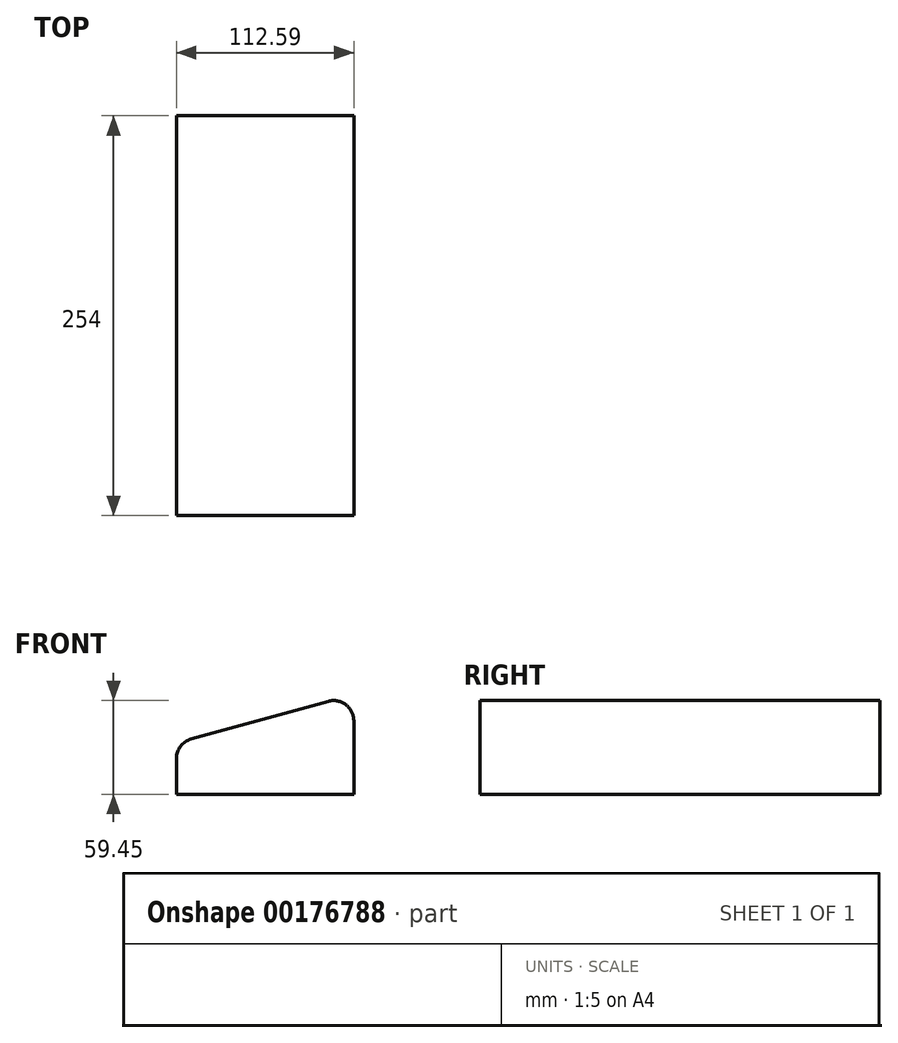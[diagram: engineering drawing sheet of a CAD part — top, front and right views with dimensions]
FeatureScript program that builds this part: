
annotation { "Feature Type Name" : "Feature", "Feature Type Description" : "" }
export const myFeature = defineFeature(function(context is Context, id is Id, definition is map)
    precondition{}
    {
        {
            var Q0;
            Q0=qCreatedBy(makeId("Front.planeOp"),FACE);
            var sketch = newSketch(context, id + "F0", { "sketchPlane" : qUnion([Q0])});
            skLineSegment(sketch, "E0", {"start": v(-38.25, 0) * mm, "end": v(-38.25, 22.78) * mm});
            skLineSegment(sketch, "E1", {"start": v(-28.92, 35.02) * mm, "end": v(58.28, 59) * mm});
            skLineSegment(sketch, "E2", {"start": v(74.34, 46.75) * mm, "end": v(74.34, 0) * mm});
            skLineSegment(sketch, "E3", {"start": v(74.34, 0) * mm, "end": v(-38.25, 0) * mm});
            skPoint(sketch, "E4.visualSharp", {"position": v(-38.25, 32.46) * mm});
            skArc(sketch, "E4.filletArc", {"start": v(-28.92, 35.02) * mm, "mid": v(-35.65, 30.48) * mm, "end": v(-38.25, 22.78) * mm});
            skPoint(sketch, "E5.visualSharp", {"position": v(74.34, 63.4) * mm});
            skArc(sketch, "E5.filletArc", {"start": v(74.34, 46.75) * mm, "mid": v(69.34, 56.85) * mm, "end": v(58.28, 59) * mm});
            skSolve(sketch);
        }
        {
            var Q0;
            Q0=makeQuery(id+"F0.imprint","IMPRINT",FACE,{"disambiguationData":[TD([[makeQuery(id+"F0.imprint","IMPRINT",EDGE,{"derivedFrom":sQuery(id+"F0.wireOp",EDGE,"E0")}),-1.0]])]});
            extrude(context, id + "F1", {"entities" : qUnion([Q0]), "depth" : 254 * mm});
        }
    });
